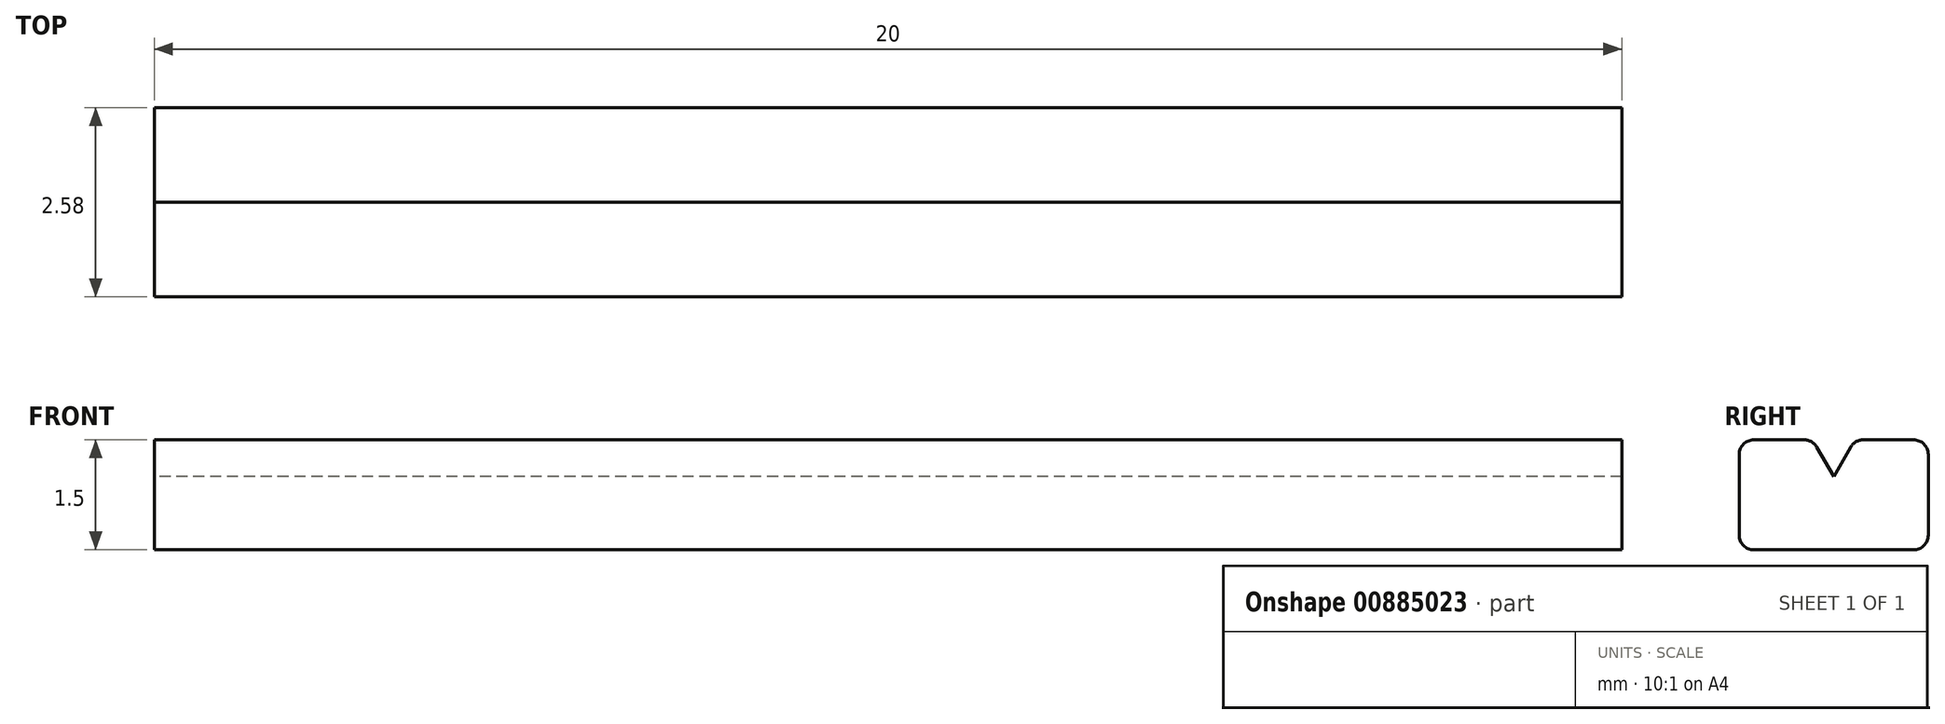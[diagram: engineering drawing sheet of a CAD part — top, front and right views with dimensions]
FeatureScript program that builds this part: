
annotation { "Feature Type Name" : "Feature", "Feature Type Description" : "" }
export const myFeature = defineFeature(function(context is Context, id is Id, definition is map)
    precondition{}
    {
        {
            var Q0;
            Q0=qCreatedBy(makeId("Right.planeOp"),FACE);
            var sketch = newSketch(context, id + "F0", { "sketchPlane" : qUnion([Q0])});
            skLineSegment(sketch, "E0", {"start": v(0, 1.5) * mm, "end": v(1, 1.5) * mm});
            skLineSegment(sketch, "E1", {"start": v(1, 1.5) * mm, "end": v(1.29, 1) * mm});
            skLineSegment(sketch, "E2", {"start": v(1.29, 1) * mm, "end": v(1.58, 1.5) * mm});
            skLineSegment(sketch, "E3", {"start": v(1.58, 1.5) * mm, "end": v(2.58, 1.5) * mm});
            skLineSegment(sketch, "E4", {"start": v(2.58, 1.5) * mm, "end": v(2.58, 0) * mm});
            skLineSegment(sketch, "E5", {"start": v(2.58, 0) * mm, "end": v(0, 0) * mm});
            skLineSegment(sketch, "E6", {"start": v(0, 1.5) * mm, "end": v(0, 0) * mm});
            skSolve(sketch);
        }
        {
            var Q0;
            Q0=makeQuery(id+"F0.imprint","IMPRINT",FACE,{"disambiguationData":[TD([[makeQuery(id+"F0.imprint","IMPRINT",EDGE,{"derivedFrom":sQuery(id+"F0.wireOp",EDGE,"E0")}),-1.0]])]});
            extrude(context, id + "F1", {"entities" : qUnion([Q0]), "depth" : 20 * mm, "offsetDistance" : 25 * mm});
        }
        {
            var Q0;
            Q0=makeQuery(id+"F1.opExtrude","SWEPT_EDGE",EDGE,{"disambiguationData":[OSD([sQuery(id+"F0.wireOp",EDGE,"E0"),sQuery(id+"F0.wireOp",EDGE,"E1")])]});
            var Q1;
            Q1=makeQuery(id+"F1.opExtrude","SWEPT_EDGE",EDGE,{"disambiguationData":[OSD([sQuery(id+"F0.wireOp",EDGE,"E0"),sQuery(id+"F0.wireOp",EDGE,"E6")])]});
            var Q2;
            Q2=makeQuery(id+"F1.opExtrude","SWEPT_EDGE",EDGE,{"disambiguationData":[OSD([sQuery(id+"F0.wireOp",EDGE,"E2"),sQuery(id+"F0.wireOp",EDGE,"E3")])]});
            var Q3;
            Q3=makeQuery(id+"F1.opExtrude","SWEPT_EDGE",EDGE,{"disambiguationData":[OSD([sQuery(id+"F0.wireOp",EDGE,"E3"),sQuery(id+"F0.wireOp",EDGE,"E4")])]});
            var Q4;
            Q4=makeQuery(id+"F1.opExtrude","SWEPT_EDGE",EDGE,{"disambiguationData":[OSD([sQuery(id+"F0.wireOp",EDGE,"E4"),sQuery(id+"F0.wireOp",EDGE,"E5")])]});
            var Q5;
            Q5=makeQuery(id+"F1.opExtrude","SWEPT_EDGE",EDGE,{"disambiguationData":[OSD([sQuery(id+"F0.wireOp",EDGE,"E5"),sQuery(id+"F0.wireOp",EDGE,"E6")])]});
            fillet(context, id + "F2", {"entities" : qUnion([Q0, Q1, Q2, Q3, Q4, Q5]), "radius" : 0.2 * mm, "tangentPropagation" : true, "allowEdgeOverflow" : false});
        }
    });
